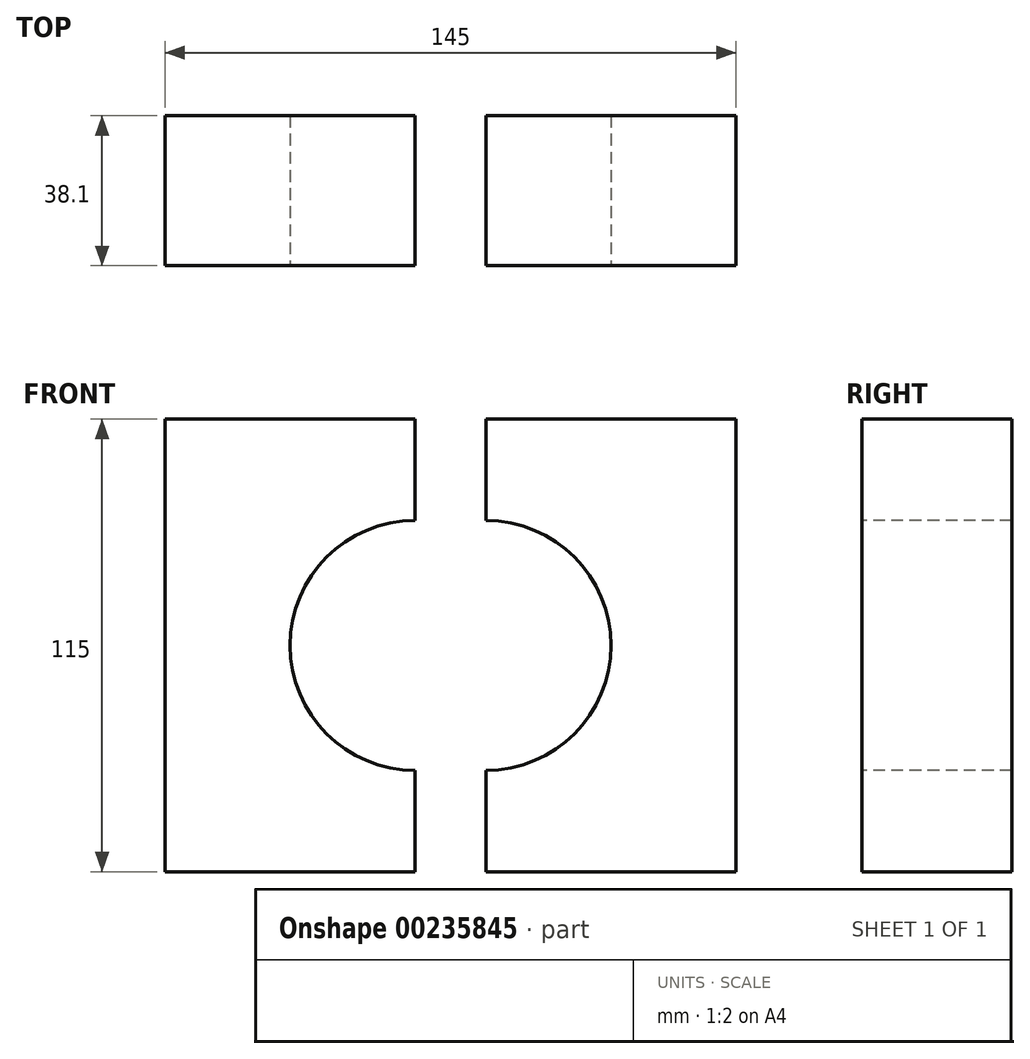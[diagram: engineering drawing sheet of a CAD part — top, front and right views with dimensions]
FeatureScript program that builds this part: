
annotation { "Feature Type Name" : "Feature", "Feature Type Description" : "" }
export const myFeature = defineFeature(function(context is Context, id is Id, definition is map)
    precondition{}
    {
        {
            var Q0;
            Q0=qCreatedBy(makeId("Front.planeOp"),FACE);
            var sketch = newSketch(context, id + "F0", { "sketchPlane" : qUnion([Q0])});
            skLineSegment(sketch, "E0.bottom", {"start": v(0, 0) * mm, "end": v(63.5, 0) * mm});
            skLineSegment(sketch, "E0.top", {"start": v(0, 115) * mm, "end": v(63.5, 115) * mm});
            skLineSegment(sketch, "E0.left", {"start": v(0, 0) * mm, "end": v(0, 115) * mm});
            skLineSegment(sketch, "E0.right", {"start": v(63.5, 0) * mm, "end": v(63.5, 115) * mm});
            skLineSegment(sketch, "E1.bottom", {"start": v(81.5, 115) * mm, "end": v(145, 115) * mm});
            skLineSegment(sketch, "E1.top", {"start": v(81.5, 0) * mm, "end": v(145, 0) * mm});
            skLineSegment(sketch, "E1.left", {"start": v(145, 115) * mm, "end": v(145, 0) * mm});
            skLineSegment(sketch, "E1.right", {"start": v(81.5, 115) * mm, "end": v(81.5, 0) * mm});
            skSolve(sketch);
        }
        {
            var Q0;
            Q0=makeQuery(id+"F0.imprint","IMPRINT",FACE,{"disambiguationData":[TD([[makeQuery(id+"F0.imprint","IMPRINT",EDGE,{"derivedFrom":sQuery(id+"F0.wireOp",EDGE,"E0.bottom")}),1.0]])]});
            var Q1;
            Q1=makeQuery(id+"F0.imprint","IMPRINT",FACE,{"disambiguationData":[TD([[makeQuery(id+"F0.imprint","IMPRINT",EDGE,{"derivedFrom":sQuery(id+"F0.wireOp",EDGE,"E1.bottom")}),-1.0]])]});
            extrude(context, id + "F1", {"entities" : qUnion([Q0, Q1]), "depth" : 38.1 * mm});
        }
        {
            var Q0;
            Q0=makeQuery(id+"F1.opExtrude","CAP_FACE",FACE,{"disambiguationData":[OSD([sQuery(id+"F0.wireOp",EDGE,"E0.bottom"),sQuery(id+"F0.wireOp",EDGE,"E0.top"),sQuery(id+"F0.wireOp",EDGE,"E0.left"),sQuery(id+"F0.wireOp",EDGE,"E0.right")])],"isStart":false});
            var sketch = newSketch(context, id + "F2", { "sketchPlane" : qUnion([Q0])});
            skCircle(sketch, "E2", {"center": v(63.5, 57.5) * mm, "radius": 31.75 * mm});
            skSolve(sketch);
        }
        {
            var Q0;
            {var subQ0=sQuery(id+"F2.wireOp",EDGE,"E2");var subQ1=makeQuery(id+"F1.opExtrude","CAP_EDGE",EDGE,{"disambiguationData":[OSD([sQuery(id+"F0.wireOp",EDGE,"E0.right")])],"isStart":false});var subQ2=makeQuery(id+"F2.imprint","INTERSECT",VERTEX,{"disambiguationData":[OD(0.0)],"derivedFrom":[subQ1,subQ0]});Q0=makeQuery(id+"F2.imprint","IMPRINT",FACE,{"disambiguationData":[TD([[makeQuery(id+"F2.imprint","IMPRINT",EDGE,{"disambiguationData":[TD([[subQ2,1.0]])],"derivedFrom":subQ0}),1.0]])]});}
            extrude(context, id + "F3", {"entities" : qUnion([Q0]), "operationType" : NewBodyOperationType.REMOVE, "oppositeDirection" : true, "depth" : 76.2 * mm});
        }
        {
            var Q0;
            Q0=makeQuery(id+"F1.opExtrude","CAP_FACE",FACE,{"disambiguationData":[OSD([sQuery(id+"F0.wireOp",EDGE,"E1.bottom"),sQuery(id+"F0.wireOp",EDGE,"E1.top"),sQuery(id+"F0.wireOp",EDGE,"E1.left"),sQuery(id+"F0.wireOp",EDGE,"E1.right")])],"isStart":false});
            var sketch = newSketch(context, id + "F4", { "sketchPlane" : qUnion([Q0])});
            skCircle(sketch, "E3", {"center": v(81.5, 57.5) * mm, "radius": 31.75 * mm});
            skSolve(sketch);
        }
        {
            var Q0;
            Q0 = qSketchRegion(id + "F4", true);
            extrude(context, id + "F5", {"entities" : qUnion([Q0]), "operationType" : NewBodyOperationType.REMOVE, "oppositeDirection" : true, "depth" : 76.2 * mm});
        }
    });
